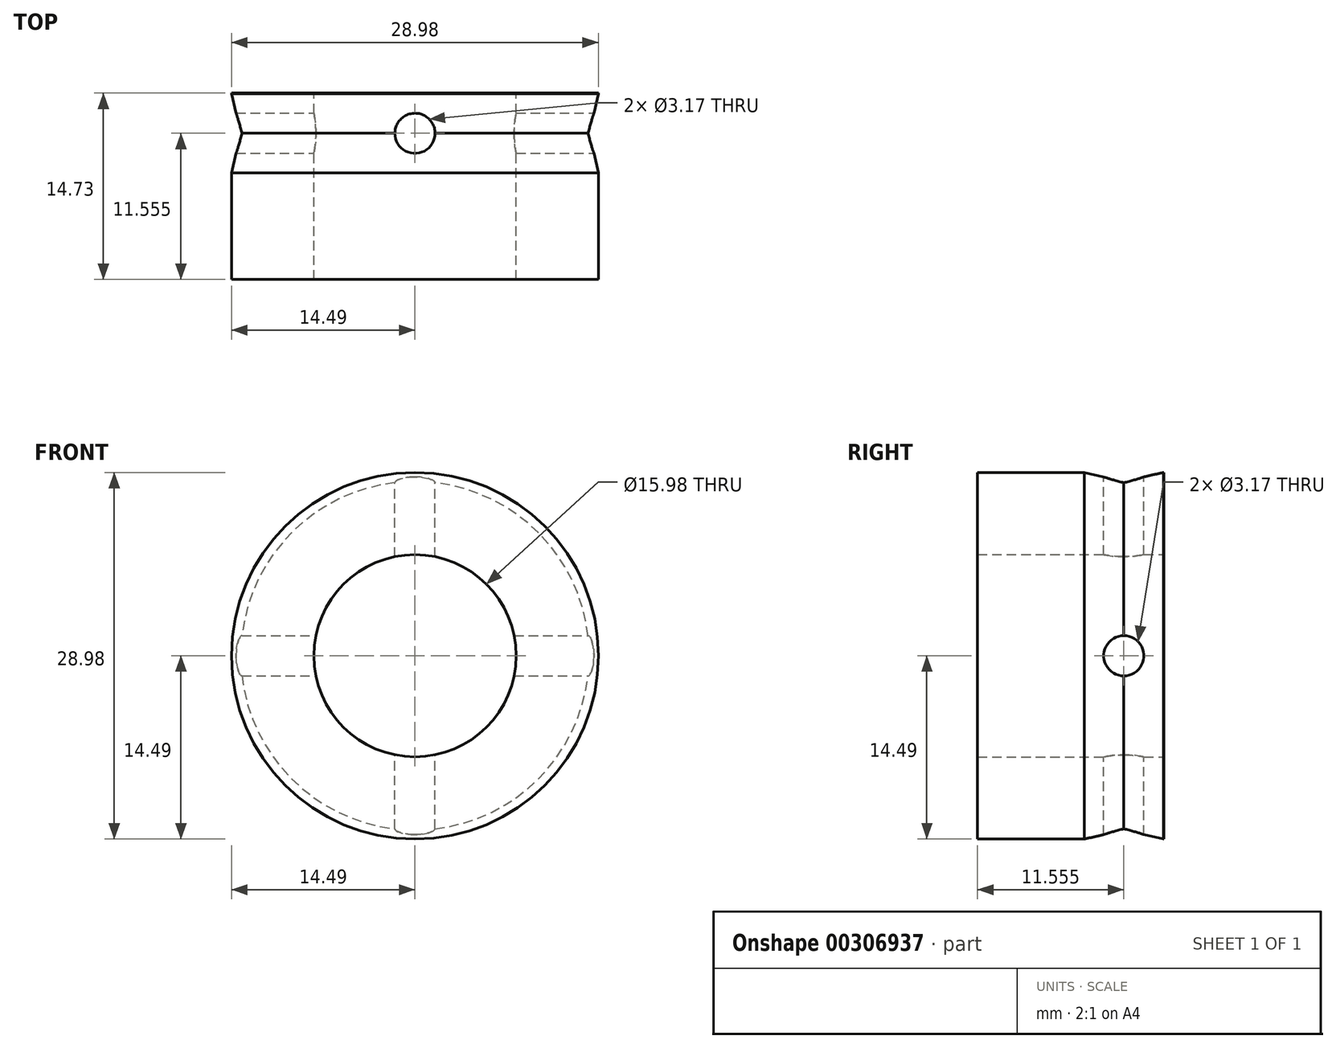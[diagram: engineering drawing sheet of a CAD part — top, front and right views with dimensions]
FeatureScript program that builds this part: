
annotation { "Feature Type Name" : "Feature", "Feature Type Description" : "" }
export const myFeature = defineFeature(function(context is Context, id is Id, definition is map)
    precondition{}
    {
        {
            var Q0;
            Q0=qCreatedBy(makeId("Front.planeOp"),FACE);
            var sketch = newSketch(context, id + "F0", { "sketchPlane" : qUnion([Q0])});
            skCircle(sketch, "E0", {"center": v(0, 0) * mm, "radius": 14.5 * mm});
            skCircle(sketch, "E1", {"center": v(0, 0) * mm, "radius": 7.99 * mm});
            skSolve(sketch);
        }
        {
            var Q0;
            Q0=makeQuery(id+"F0.imprint","IMPRINT",FACE,{"disambiguationData":[TD([[makeQuery(id+"F0.imprint","IMPRINT",EDGE,{"derivedFrom":sQuery(id+"F0.wireOp",EDGE,"E0")}),1.0]])]});
            extrude(context, id + "F1", {"entities" : qUnion([Q0]), "depth" : 6.35 * mm});
        }
        {
            var Q0;
            Q0=makeQuery(id+"F1.opExtrude","CAP_FACE",FACE,{"disambiguationData":[OSD([sQuery(id+"F0.wireOp",EDGE,"E0")])],"isStart":false});
            var sketch = newSketch(context, id + "F2", { "sketchPlane" : qUnion([Q0])});
            skCircle(sketch, "E2", {"center": v(0, 0) * mm, "radius": 14.5 * mm});
            skSolve(sketch);
        }
        {
            var Q0;
            Q0=makeQuery(id+"F2.imprint","IMPRINT",FACE,{"disambiguationData":[TD([[makeQuery(id+"F2.imprint","IMPRINT",EDGE,{"derivedFrom":makeQuery(id+"F1.opExtrude","CAP_EDGE",EDGE,{"disambiguationData":[OSD([sQuery(id+"F0.wireOp",EDGE,"E0")])],"isStart":false})}),1.0]])]});
            var Q1;
            Q1=makeQuery(id+"F2.imprint","IMPRINT",FACE,{"disambiguationData":[TD([[makeQuery(id+"F2.imprint","IMPRINT",EDGE,{"derivedFrom":sQuery(id+"F2.wireOp",EDGE,"E2")}),1.0]])]});
            extrude(context, id + "F3", {"entities" : qUnion([Q0, Q1]), "operationType" : NewBodyOperationType.ADD, "depth" : 8.38 * mm});
        }
        {
            var Q0;
            Q0=qCreatedBy(makeId("Right.planeOp"),FACE);
            var sketch = newSketch(context, id + "F4", { "sketchPlane" : qUnion([Q0])});
            skCircle(sketch, "E3", {"center": v(-3.18, 0) * mm, "radius": 1.59 * mm});
            skSolve(sketch);
        }
        {
            var Q0;
            Q0=makeQuery(id+"F4.imprint","IMPRINT",FACE,{"disambiguationData":[TD([[makeQuery(id+"F4.imprint","IMPRINT",EDGE,{"derivedFrom":sQuery(id+"F4.wireOp",EDGE,"E3")}),1.0]])]});
            extrude(context, id + "F5", {"entities" : qUnion([Q0]), "operationType" : NewBodyOperationType.REMOVE, "endBound" : BoundingType.SYMMETRIC, "oppositeDirection" : true, "depth" : 30.33 * mm});
        }
        {
            var Q0;
            Q0=qCreatedBy(makeId("Top.planeOp"),FACE);
            var sketch = newSketch(context, id + "F6", { "sketchPlane" : qUnion([Q0])});
            skCircle(sketch, "E4", {"center": v(0, -3.18) * mm, "radius": 1.59 * mm});
            skSolve(sketch);
        }
        {
            var Q0;
            Q0=makeQuery(id+"F6.imprint","IMPRINT",FACE,{"disambiguationData":[TD([[makeQuery(id+"F6.imprint","IMPRINT",EDGE,{"derivedFrom":sQuery(id+"F6.wireOp",EDGE,"E4")}),1.0]])]});
            extrude(context, id + "F7", {"entities" : qUnion([Q0]), "operationType" : NewBodyOperationType.REMOVE, "endBound" : BoundingType.SYMMETRIC, "oppositeDirection" : true, "depth" : 30.84 * mm});
        }
        {
            var Q0;
            Q0=qCreatedBy(makeId("Right.planeOp"),FACE);
            var sketch = newSketch(context, id + "F8", { "sketchPlane" : qUnion([Q0])});
            skLineSegment(sketch, "E5", {"start": v(0, 16.05) * mm, "end": v(-6.35, 16.05) * mm});
            skLineSegment(sketch, "E6", {"start": v(-6.35, 14.5) * mm, "end": v(-6.35, 16.05) * mm});
            skLineSegment(sketch, "E7", {"start": v(-3.18, 16.48) * mm, "end": v(-3.18, 13.77) * mm, "construction": true});
            skPoint(sketch, "E7.startSnap0", {"position": v(-3.18, 16.05) * mm});
            skLineSegment(sketch, "E8", {"start": v(-6.35, 14.5) * mm, "end": v(-3.18, 13.77) * mm});
            skLineSegment(sketch, "E9", {"start": v(0, 14.5) * mm, "end": v(-3.18, 13.77) * mm});
            skLineSegment(sketch, "E10", {"start": v(0, 14.5) * mm, "end": v(0, 16.05) * mm});
            skSolve(sketch);
        }
        {
            var Q0;
            Q0=makeQuery(id+"F8.imprint","IMPRINT",FACE,{"disambiguationData":[TD([[makeQuery(id+"F8.imprint","IMPRINT",EDGE,{"derivedFrom":sQuery(id+"F8.wireOp",EDGE,"E5")}),1.0]])]});
            var Q1;
            Q1=sQuery(id+"F0.wireOp",EDGE,"E0");
            sweep(context, id + "F9", {"operationType" : NewBodyOperationType.REMOVE, "profiles" : qUnion([Q0]), "path" : qUnion([Q1])});
        }
    });
